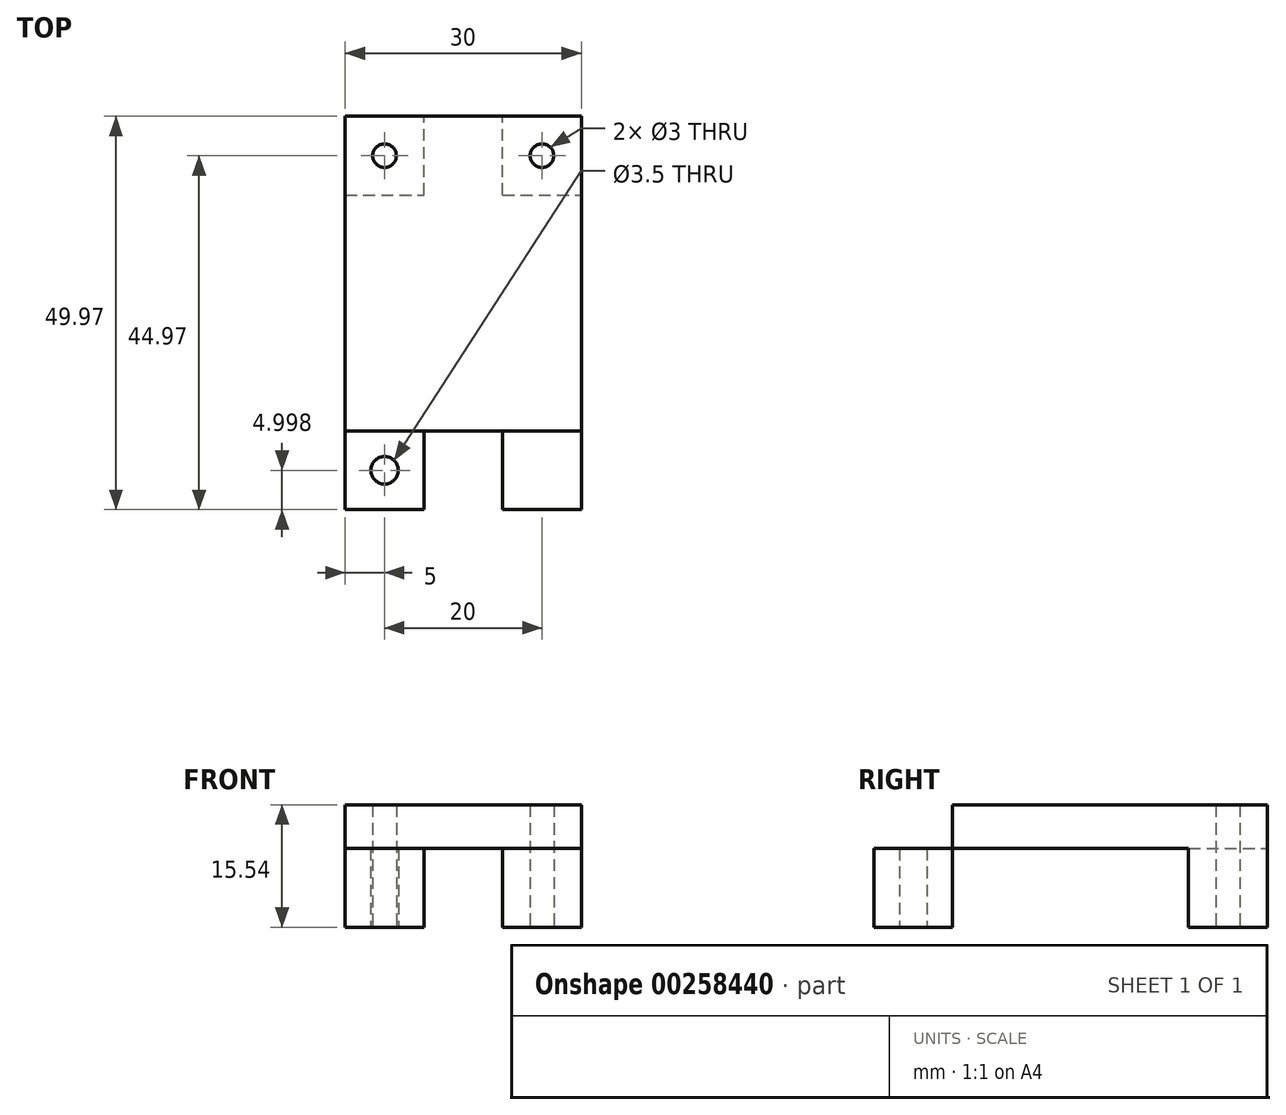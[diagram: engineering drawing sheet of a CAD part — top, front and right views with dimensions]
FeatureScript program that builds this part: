
annotation { "Feature Type Name" : "Feature", "Feature Type Description" : "" }
export const myFeature = defineFeature(function(context is Context, id is Id, definition is map)
    precondition{}
    {
        {
            var Q0;
            Q0=qCreatedBy(makeId("Front.planeOp"),FACE);
            var sketch = newSketch(context, id + "F0", { "sketchPlane" : qUnion([Q0])});
            skLineSegment(sketch, "E0.rect.top", {"start": v(5, 5) * mm, "end": v(-5, 5) * mm});
            skLineSegment(sketch, "E0.rect.left", {"start": v(5, -5) * mm, "end": v(5, 5) * mm});
            skLineSegment(sketch, "E0.rect.right", {"start": v(-5, -5) * mm, "end": v(-5, 5) * mm});
            skPoint(sketch, "E0.rect.middle", {"position": v(0, 0) * mm});
            skLineSegment(sketch, "E1", {"start": v(-15, 5) * mm, "end": v(-15, 7.74) * mm});
            skLineSegment(sketch, "E2.MirrorCS", {"start": v(15, 5) * mm, "end": v(15, 7.74) * mm});
            skLineSegment(sketch, "E3", {"start": v(-10.61, 10.54) * mm, "end": v(0, 10.54) * mm});
            skLineSegment(sketch, "E4.MirrorCS", {"start": v(10.61, 10.54) * mm, "end": v(0, 10.54) * mm});
            skLineSegment(sketch, "E5", {"start": v(-15, 5) * mm, "end": v(-15, -5) * mm});
            skLineSegment(sketch, "E6", {"start": v(-15, -5) * mm, "end": v(-5, -5) * mm});
            skLineSegment(sketch, "E7.MirrorCS", {"start": v(15, 5) * mm, "end": v(15, -5) * mm});
            skLineSegment(sketch, "E8.MirrorCS", {"start": v(15, -5) * mm, "end": v(5, -5) * mm});
            skPoint(sketch, "E9.orphan", {"position": v(0, 7.74) * mm});
            skPoint(sketch, "E10.MirrorCS.end.orphan", {"position": v(10.61, 10.54) * mm});
            skPoint(sketch, "E10.MirrorCS.start.orphan", {"position": v(10.61, 7.74) * mm});
            skPoint(sketch, "E11.start.orphan", {"position": v(-10.61, 7.74) * mm});
            skPoint(sketch, "E12.MirrorCS.end.orphan", {"position": v(12.8, 7.74) * mm});
            skPoint(sketch, "E12.MirrorCS.start.orphan", {"position": v(15, 7.74) * mm});
            skPoint(sketch, "E13.MirrorCS.end.orphan", {"position": v(-12.8, 7.74) * mm});
            skPoint(sketch, "E13.MirrorCS.start.orphan", {"position": v(-10.61, 10.54) * mm});
            skLineSegment(sketch, "E14", {"start": v(-15, 7.74) * mm, "end": v(-15, 10.54) * mm});
            skLineSegment(sketch, "E15", {"start": v(-15, 10.54) * mm, "end": v(-10.61, 10.54) * mm});
            skLineSegment(sketch, "E16", {"start": v(10.61, 10.54) * mm, "end": v(15, 10.54) * mm});
            skLineSegment(sketch, "E17", {"start": v(15, 10.54) * mm, "end": v(15, 7.74) * mm});
            skLineSegment(sketch, "E18", {"start": v(-5, -5) * mm, "end": v(5, -5) * mm, "construction": true});
            skLineSegment(sketch, "E19", {"start": v(-5, 5) * mm, "end": v(5, -5) * mm, "construction": true});
            skLineSegment(sketch, "E20", {"start": v(5, 5) * mm, "end": v(-5, -5) * mm, "construction": true});
            skSolve(sketch);
        }
        {
            var Q0;
            Q0=makeQuery(id+"F0.imprint","IMPRINT",FACE,{"disambiguationData":[TD([[makeQuery(id+"F0.imprint","IMPRINT",EDGE,{"derivedFrom":sQuery(id+"F0.wireOp",EDGE,"E0.rect.top")}),-1.0]])]});
            extrude(context, id + "F1", {"entities" : qUnion([Q0]), "depth" : 10 * mm});
        }
        {
            var Q0;
            Q0=makeQuery(id+"F1.opExtrude","SWEPT_FACE",FACE,{"disambiguationData":[OSD([sQuery(id+"F0.wireOp",EDGE,"E8.MirrorCS")])]});
            var sketch = newSketch(context, id + "F2", { "sketchPlane" : qUnion([Q0])});
            skCircle(sketch, "E21", {"center": v(10, 5) * mm, "radius": 1.5 * mm});
            skCircle(sketch, "E22.MirrorC", {"center": v(-10, 5) * mm, "radius": 1.5 * mm});
            skSolve(sketch);
        }
        {
            var Q0;
            Q0=qSketchRegion(id+"F2",true);
            extrude(context, id + "F3", {"entities" : qUnion([Q0]), "operationType" : NewBodyOperationType.REMOVE, "oppositeDirection" : true, "depth" : 16 * mm});
        }
        {
            var Q0;
            Q0=makeQuery(id+"F1.opExtrude","CAP_FACE",FACE,{"disambiguationData":[OSD([sQuery(id+"F0.wireOp",EDGE,"E0.rect.top"),sQuery(id+"F0.wireOp",EDGE,"E0.rect.left"),sQuery(id+"F0.wireOp",EDGE,"E0.rect.right"),sQuery(id+"F0.wireOp",EDGE,"E1"),sQuery(id+"F0.wireOp",EDGE,"E2.MirrorCS"),sQuery(id+"F0.wireOp",EDGE,"E3"),sQuery(id+"F0.wireOp",EDGE,"E4.MirrorCS"),sQuery(id+"F0.wireOp",EDGE,"E5"),sQuery(id+"F0.wireOp",EDGE,"E6"),sQuery(id+"F0.wireOp",EDGE,"E7.MirrorCS"),sQuery(id+"F0.wireOp",EDGE,"E8.MirrorCS"),sQuery(id+"F0.wireOp",EDGE,"E14"),sQuery(id+"F0.wireOp",EDGE,"E15"),sQuery(id+"F0.wireOp",EDGE,"E16"),sQuery(id+"F0.wireOp",EDGE,"E17")])],"isStart":false});
            cPlane(context, id + "F4", {"entities" : qUnion([Q0]), "cplaneType" : CPlaneType.OFFSET, "offset" : 0 * mm, "width" : 150 * mm, "height" : 150 * mm});
        }
        {
            var Q0;
            Q0=makeQuery(id+"F1.opExtrude","SWEPT_FACE",FACE,{"disambiguationData":[OSD([sQuery(id+"F0.wireOp",EDGE,"E3"),sQuery(id+"F0.wireOp",EDGE,"E4.MirrorCS"),sQuery(id+"F0.wireOp",EDGE,"E15"),sQuery(id+"F0.wireOp",EDGE,"E16")])]});
            var sketch = newSketch(context, id + "F5", { "sketchPlane" : qUnion([Q0])});
            skLineSegment(sketch, "E23.bottom", {"start": v(-15, -10) * mm, "end": v(15, -10) * mm});
            skLineSegment(sketch, "E23.top", {"start": v(-15, -39.97) * mm, "end": v(15, -39.97) * mm});
            skLineSegment(sketch, "E23.left", {"start": v(-15, -10) * mm, "end": v(-15, -39.97) * mm});
            skLineSegment(sketch, "E23.right", {"start": v(15, -10) * mm, "end": v(15, -39.97) * mm});
            skLineSegment(sketch, "E24.bottom", {"start": v(15, -39.97) * mm, "end": v(-15, -39.97) * mm});
            skLineSegment(sketch, "E24.top", {"start": v(15, -49.97) * mm, "end": v(-15, -49.97) * mm});
            skLineSegment(sketch, "E24.left", {"start": v(15, -39.97) * mm, "end": v(15, -49.97) * mm});
            skLineSegment(sketch, "E24.right", {"start": v(-15, -39.97) * mm, "end": v(-15, -49.97) * mm});
            skLineSegment(sketch, "E25", {"start": v(-10, -5) * mm, "end": v(-10, -49.97) * mm, "construction": true});
            skLineSegment(sketch, "E26", {"start": v(10, -5) * mm, "end": v(10, -49.97) * mm, "construction": true});
            skLineSegment(sketch, "E27", {"start": v(-15, -5) * mm, "end": v(15, -5) * mm, "construction": true});
            skLineSegment(sketch, "E28", {"start": v(-15, -44.97) * mm, "end": v(15, -44.97) * mm, "construction": true});
            skCircle(sketch, "E29", {"center": v(-10, -44.97) * mm, "radius": 1.5 * mm});
            skCircle(sketch, "E30", {"center": v(10, -44.97) * mm, "radius": 1.5 * mm});
            skSolve(sketch);
        }
        {
            var Q0;
            Q0=makeQuery(id+"F5.imprint","IMPRINT",FACE,{"disambiguationData":[TD([[makeQuery(id+"F5.imprint","IMPRINT",EDGE,{"derivedFrom":sQuery(id+"F5.wireOp",EDGE,"E23.bottom")}),-1.0]])]});
            var Q1;
            Q1=makeQuery(id+"F5.imprint","IMPRINT",FACE,{"disambiguationData":[TD([[makeQuery(id+"F5.imprint","IMPRINT",EDGE,{"derivedFrom":sQuery(id+"F5.wireOp",EDGE,"E24.bottom")}),1.0]])]});
            extrude(context, id + "F6", {"entities" : qUnion([Q0, Q1]), "operationType" : NewBodyOperationType.ADD, "oppositeDirection" : true, "depth" : 5.54 * mm});
        }
        {
            var Q0;
            Q0=makeQuery(id+"F6.boolean.opBoolean","MERGE",FACE,{"derivedFrom":[makeQuery(id+"F1.opExtrude","SWEPT_FACE",FACE,{"disambiguationData":[OSD([sQuery(id+"F0.wireOp",EDGE,"E0.rect.top")])]}),makeQuery(id+"F6.opExtrude","CAP_FACE",FACE,{"disambiguationData":[OSD([sQuery(id+"F5.wireOp",EDGE,"E23.bottom"),sQuery(id+"F5.wireOp",EDGE,"E23.left"),sQuery(id+"F5.wireOp",EDGE,"E23.right"),sQuery(id+"F5.wireOp",EDGE,"E24.top"),sQuery(id+"F5.wireOp",EDGE,"E24.left"),sQuery(id+"F5.wireOp",EDGE,"E24.right"),sQuery(id+"F5.wireOp",EDGE,"E29"),sQuery(id+"F5.wireOp",EDGE,"E30")])],"isStart":false})]});
            var sketch = newSketch(context, id + "F7", { "sketchPlane" : qUnion([Q0])});
            skLineSegment(sketch, "E31.bottom", {"start": v(15, 49.97) * mm, "end": v(5, 49.97) * mm});
            skLineSegment(sketch, "E31.top", {"start": v(15, 39.97) * mm, "end": v(5, 39.97) * mm});
            skLineSegment(sketch, "E31.left", {"start": v(15, 49.97) * mm, "end": v(15, 39.97) * mm});
            skLineSegment(sketch, "E31.right", {"start": v(5, 49.97) * mm, "end": v(5, 39.97) * mm});
            skLineSegment(sketch, "E32", {"start": v(0, 49.97) * mm, "end": v(0, 0) * mm, "construction": true});
            skLineSegment(sketch, "E33.MirrorCS", {"start": v(-15, 39.97) * mm, "end": v(-5, 39.97) * mm});
            skLineSegment(sketch, "E34.MirrorCS", {"start": v(-5, 49.97) * mm, "end": v(-5, 39.97) * mm});
            skLineSegment(sketch, "E35.MirrorCS", {"start": v(-15, 49.97) * mm, "end": v(-15, 39.97) * mm});
            skLineSegment(sketch, "E36.MirrorCS", {"start": v(-15, 49.97) * mm, "end": v(-5, 49.97) * mm});
            skSolve(sketch);
        }
        {
            var Q0;
            Q0 = qSketchRegion(id + "F7", true);
            extrude(context, id + "F8", {"entities" : qUnion([Q0]), "operationType" : NewBodyOperationType.ADD, "depth" : 10 * mm});
        }
        {
            var Q0;
            Q0=makeQuery(id+"F8.opExtrude","CAP_FACE",FACE,{"disambiguationData":[OSD([sQuery(id+"F7.wireOp",EDGE,"E33.MirrorCS"),sQuery(id+"F7.wireOp",EDGE,"E34.MirrorCS"),sQuery(id+"F7.wireOp",EDGE,"E35.MirrorCS"),sQuery(id+"F7.wireOp",EDGE,"E36.MirrorCS")])],"isStart":false});
            var sketch = newSketch(context, id + "F9", { "sketchPlane" : qUnion([Q0])});
            skLineSegment(sketch, "E37", {"start": v(-15, 44.97) * mm, "end": v(15.72, 44.97) * mm, "construction": true});
            skPoint(sketch, "E37.endSnap0", {"position": v(-5, 44.97) * mm});
            skLineSegment(sketch, "E38", {"start": v(-10, 49.97) * mm, "end": v(-10, 39.97) * mm, "construction": true});
            skCircle(sketch, "E39", {"center": v(-10, 44.97) * mm, "radius": 1.75 * mm});
            skCircle(sketch, "E40.MirrorC", {"center": v(10, 44.97) * mm, "radius": 1.75 * mm});
            skSolve(sketch);
        }
        {
            var Q0;
            Q0=makeQuery(id+"F9.imprint","IMPRINT",FACE,{"disambiguationData":[TD([[makeQuery(id+"F9.imprint","IMPRINT",EDGE,{"derivedFrom":sQuery(id+"F9.wireOp",EDGE,"E39")}),1.0]])]});
            var Q1;
            Q1=makeQuery(id+"F9.imprint","IMPRINT",FACE,{"disambiguationData":[TD([[makeQuery(id+"F9.imprint","IMPRINT",EDGE,{"derivedFrom":sQuery(id+"F9.wireOp",EDGE,"E40.MirrorC")}),-1.0]])]});
            extrude(context, id + "F10", {"entities" : qUnion([Q0, Q1]), "operationType" : NewBodyOperationType.REMOVE, "oppositeDirection" : true, "depth" : 25 * mm});
        }
    });
